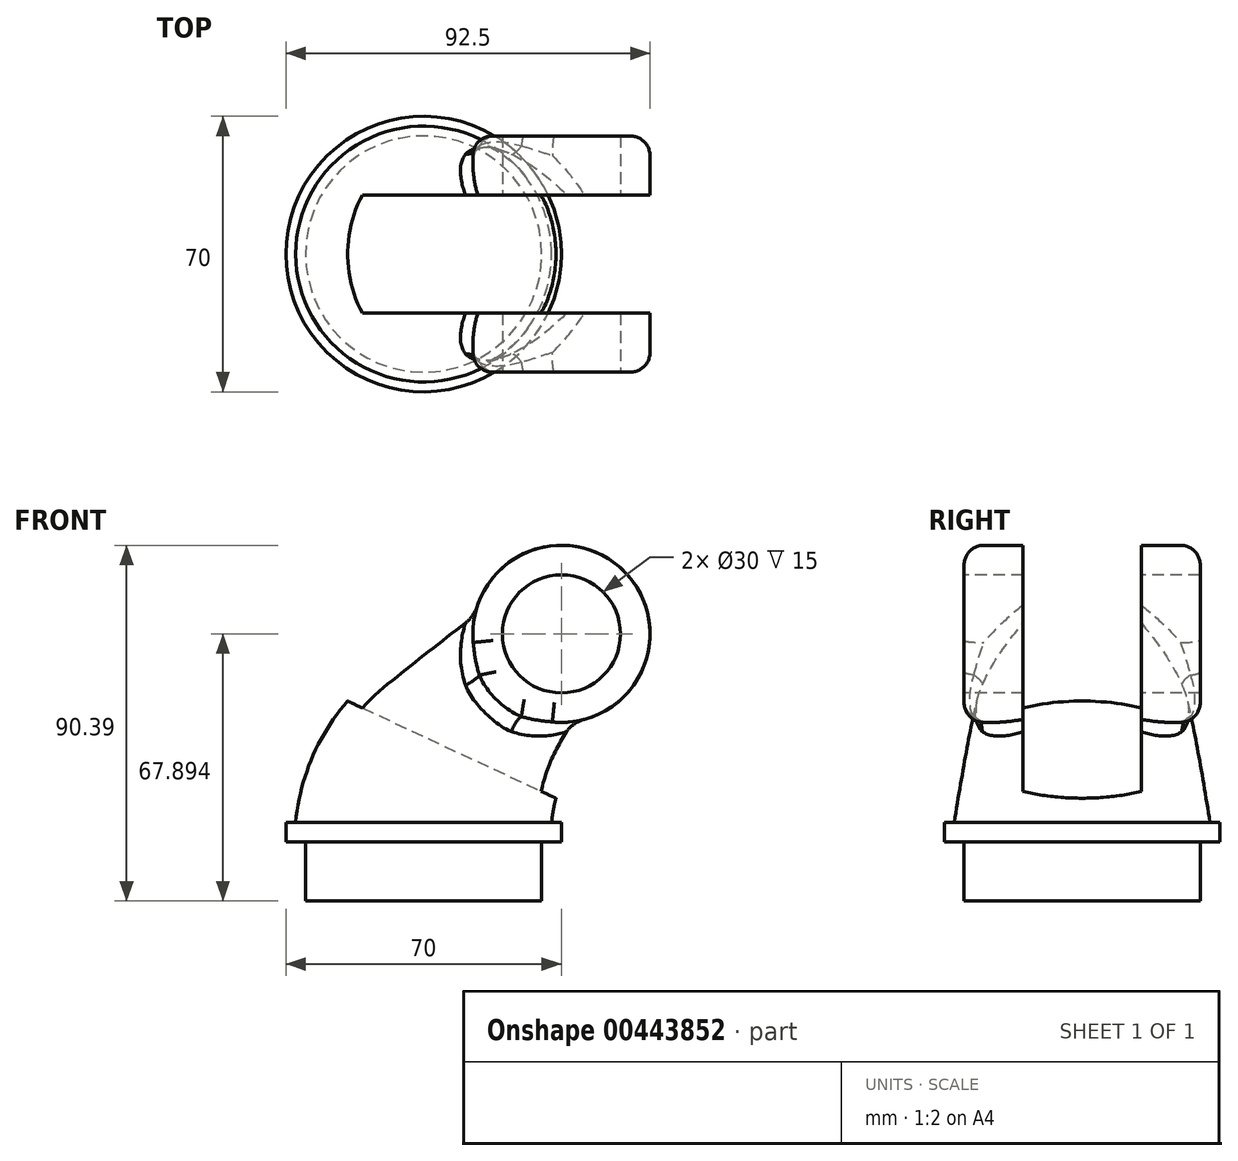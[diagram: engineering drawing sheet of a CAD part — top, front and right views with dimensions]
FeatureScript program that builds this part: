
annotation { "Feature Type Name" : "Feature", "Feature Type Description" : "" }
export const myFeature = defineFeature(function(context is Context, id is Id, definition is map)
    precondition{}
    {
        {
            var Q0;
            Q0=qCreatedBy(makeId("Top.planeOp"),FACE);
            var sketch = newSketch(context, id + "F0", { "sketchPlane" : qUnion([Q0])});
            skCircle(sketch, "E0", {"center": v(0, 0) * mm, "radius": 35 * mm});
            skSolve(sketch);
        }
        {
            var Q0;
            Q0 = qSketchRegion(id + "F0", true);
            extrude(context, id + "F1", {"entities" : qUnion([Q0]), "depth" : 5 * mm});
        }
        {
            var Q0;
            Q0=qCreatedBy(makeId("Front.planeOp"),FACE);
            var sketch = newSketch(context, id + "F2", { "sketchPlane" : qUnion([Q0])});
            skArc(sketch, "E1", {"start": v(17.6, 38.3) * mm, "mid": v(5.55, 23.37) * mm, "end": v(0, 5) * mm});
            skLineSegment(sketch, "E2", {"start": v(17.6, 38.3) * mm, "end": v(35, 52.9) * mm});
            skSolve(sketch);
        }
        {
            var Q0;
            Q0=sQuery(id+"F2.wireOp",VERTEX,"E2.end");
            var Q1;
            Q1=sQuery(id+"F2.wireOp",EDGE,"E2");
            cPlane(context, id + "F3", {"entities" : qUnion([Q0, Q1]), "cplaneType" : CPlaneType.LINE_POINT, "offset" : 25 * mm, "width" : 150 * mm, "height" : 150 * mm});
        }
        {
            var Q0;
            Q0=qCreatedBy(id+"F3.planeOp",FACE);
            var sketch = newSketch(context, id + "F4", { "sketchPlane" : qUnion([Q0])});
            skCircle(sketch, "E3", {"center": v(0, 18.02) * mm, "radius": 22.5 * mm});
            skSolve(sketch);
        }
        {
            var Q0;
            Q0=makeQuery(id+"F1.opExtrude","CAP_FACE",FACE,{"disambiguationData":[OSD([sQuery(id+"F0.wireOp",EDGE,"E0")])],"isStart":false});
            var sketch = newSketch(context, id + "F5", { "sketchPlane" : qUnion([Q0])});
            skCircle(sketch, "E4", {"center": v(0, 0) * mm, "radius": 32.5 * mm});
            skSolve(sketch);
        }
        {
            var Q0;
            Q0=qCreatedBy(makeId("Front.planeOp"),FACE);
            var sketch = newSketch(context, id + "F6", { "sketchPlane" : qUnion([Q0])});
            skArc(sketch, "E5", {"start": v(-13.25, 41.78) * mm, "mid": v(-26.5, 25.3) * mm, "end": v(-32.5, 5) * mm});
            skLineSegment(sketch, "E6", {"start": v(-13.25, 41.78) * mm, "end": v(20.54, 70.13) * mm});
            skSolve(sketch);
        }
        {
            var Q0;
            Q0=qCreatedBy(makeId("Front.planeOp"),FACE);
            var sketch = newSketch(context, id + "F7", { "sketchPlane" : qUnion([Q0])});
            skArc(sketch, "E7", {"start": v(48.46, 34.82) * mm, "mid": v(37.6, 21.45) * mm, "end": v(32.5, 5) * mm});
            skLineSegment(sketch, "E8", {"start": v(48.46, 34.82) * mm, "end": v(49.46, 35.66) * mm});
            skSolve(sketch);
        }
        {
            var Q1;
            Q1=makeQuery(id+"F4.imprint","IMPRINT",FACE,{"disambiguationData":[TD([[makeQuery(id+"F4.imprint","IMPRINT",EDGE,{"derivedFrom":sQuery(id+"F4.wireOp",EDGE,"E3")}),1.0]])]});
            var Q2;
            Q2=makeQuery(id+"F5.imprint","IMPRINT",FACE,{"disambiguationData":[TD([[makeQuery(id+"F5.imprint","IMPRINT",EDGE,{"derivedFrom":sQuery(id+"F5.wireOp",EDGE,"E4")}),1.0]])]});
            var Q3;
            Q3 = qConstructionFilter(qBodyType(qCreatedBy(id + "F7" ,EDGE), BodyType.WIRE), ConstructionObject.NO);
            var Q4;
            Q4 = qConstructionFilter(qBodyType(qCreatedBy(id + "F6" ,EDGE), BodyType.WIRE), ConstructionObject.NO);
            loft(context, id + "F8", {"operationType" : NewBodyOperationType.ADD, "addGuides" : true, "sheetProfilesArray" : [{ "sheetProfileEntities" : qUnion([Q1]) }, { "sheetProfileEntities" : qUnion([Q2]) }], "guidesArray" : [{ "guideEntities" : qUnion([Q3]), "guideDerivativeType" : LoftGuideDerivativeType.DEFAULT, "guideDerivativeMagnitude" : 1 }, { "guideEntities" : qUnion([Q4]), "guideDerivativeType" : LoftGuideDerivativeType.DEFAULT, "guideDerivativeMagnitude" : 1 }]});
        }
        {
            var Q0;
            Q0=qCreatedBy(makeId("Front.planeOp"),FACE);
            var sketch = newSketch(context, id + "F9", { "sketchPlane" : qUnion([Q0])});
            skCircle(sketch, "E9", {"center": v(35, 52.9) * mm, "radius": 22.5 * mm});
            skSolve(sketch);
        }
        {
            var Q0;
            Q0 = qSketchRegion(id + "F9", true);
            extrude(context, id + "F10", {"entities" : qUnion([Q0]), "operationType" : NewBodyOperationType.ADD, "endBound" : BoundingType.SYMMETRIC, "depth" : 60 * mm});
        }
        {
            var Q0;
            Q0=makeQuery(id+"F10.boolean.opBoolean","INTERSECT",EDGE,{"disambiguationData":[OD(0.0)],"derivedFrom":[makeQuery(id+"F8.opLoft","SWEPT_FACE",FACE,{"disambiguationData":[OSD([sQuery(id+"F4.wireOp",EDGE,"E3"),sQuery(id+"F5.wireOp",EDGE,"E4"),sQuery(id+"F6.wireOp",VERTEX,"E6.start"),sQuery(id+"F6.wireOp",EDGE,"E5"),sQuery(id+"F6.wireOp",EDGE,"E6"),sQuery(id+"F7.wireOp",VERTEX,"E8.start"),sQuery(id+"F7.wireOp",EDGE,"E7"),sQuery(id+"F7.wireOp",EDGE,"E8")])]}),makeQuery(id+"F10.opExtrude","SWEPT_FACE",FACE,{"disambiguationData":[OSD([sQuery(id+"F9.wireOp",EDGE,"E9")])]})]});
            var Q1;
            Q1=makeQuery(id+"F10.boolean.opBoolean","INTERSECT",EDGE,{"disambiguationData":[OD(1.0)],"derivedFrom":[makeQuery(id+"F8.opLoft","SWEPT_FACE",FACE,{"disambiguationData":[OSD([sQuery(id+"F4.wireOp",EDGE,"E3"),sQuery(id+"F5.wireOp",EDGE,"E4"),sQuery(id+"F6.wireOp",VERTEX,"E6.start"),sQuery(id+"F6.wireOp",EDGE,"E5"),sQuery(id+"F6.wireOp",EDGE,"E6"),sQuery(id+"F7.wireOp",VERTEX,"E8.start"),sQuery(id+"F7.wireOp",EDGE,"E7"),sQuery(id+"F7.wireOp",EDGE,"E8")])]}),makeQuery(id+"F10.opExtrude","SWEPT_FACE",FACE,{"disambiguationData":[OSD([sQuery(id+"F9.wireOp",EDGE,"E9")])]})]});
            fillet(context, id + "F11", {"entities" : qUnion([Q0, Q1]), "radius" : 5 * mm, "tangentPropagation" : true, "allowEdgeOverflow" : false});
        }
        {
            var Q0;
            Q0=makeQuery(id+"F10.opExtrude","CAP_EDGE",EDGE,{"disambiguationData":[OSD([sQuery(id+"F9.wireOp",EDGE,"E9")])],"isStart":false});
            var Q1;
            Q1=makeQuery(id+"F10.opExtrude","CAP_EDGE",EDGE,{"disambiguationData":[OSD([sQuery(id+"F9.wireOp",EDGE,"E9")])],"isStart":true});
            var Q2;
            Q2=makeQuery(id+"F10.opExtrude","CAP_FACE",FACE,{"disambiguationData":[OSD([sQuery(id+"F9.wireOp",EDGE,"E9")])],"isStart":false});
            fillet(context, id + "F12", {"entities" : qUnion([Q0, Q1, Q2]), "radius" : 5 * mm, "tangentPropagation" : true, "allowEdgeOverflow" : false});
        }
        {
            var Q0;
            Q0=makeQuery(id+"F10.opExtrude","CAP_FACE",FACE,{"disambiguationData":[OSD([sQuery(id+"F9.wireOp",EDGE,"E9")])],"isStart":false});
            var sketch = newSketch(context, id + "F13", { "sketchPlane" : qUnion([Q0])});
            skCircle(sketch, "E10", {"center": v(35, 52.9) * mm, "radius": 15 * mm});
            skSolve(sketch);
        }
        {
            var Q0;
            Q0 = qSketchRegion(id + "F13", true);
            extrude(context, id + "F14", {"entities" : qUnion([Q0]), "operationType" : NewBodyOperationType.REMOVE, "endBound" : BoundingType.THROUGH_ALL, "oppositeDirection" : true, "depth" : 25 * mm});
        }
        {
            var Q0;
            Q0=qCreatedBy(makeId("Front.planeOp"),FACE);
            var sketch = newSketch(context, id + "F15", { "sketchPlane" : qUnion([Q0])});
            skLineSegment(sketch, "E11", {"start": v(-104.18, 75.4) * mm, "end": v(57.5, 0) * mm});
            skLineSegment(sketch, "E12", {"start": v(57.5, 75.4) * mm, "end": v(57.5, 0) * mm});
            skLineSegment(sketch, "E13", {"start": v(-104.18, 75.4) * mm, "end": v(57.5, 75.4) * mm});
            skSolve(sketch);
        }
        {
            var Q0;
            Q0=makeQuery(id+"F15.imprint","IMPRINT",FACE,{"disambiguationData":[TD([[makeQuery(id+"F15.imprint","IMPRINT",EDGE,{"derivedFrom":sQuery(id+"F15.wireOp",EDGE,"E11")}),1.0]])]});
            extrude(context, id + "F16", {"entities" : qUnion([Q0]), "operationType" : NewBodyOperationType.REMOVE, "endBound" : BoundingType.SYMMETRIC, "oppositeDirection" : true, "depth" : 30 * mm});
        }
        {
            var Q0;
            Q0=qCreatedBy(makeId("Front.planeOp"),FACE);
            var sketch = newSketch(context, id + "F17", { "sketchPlane" : qUnion([Q0])});
            skPoint(sketch, "E14.middle", {"position": v(0, 0) * mm});
            skLineSegment(sketch, "E15.bottom", {"start": v(0, 0) * mm, "end": v(-30, 0) * mm});
            skLineSegment(sketch, "E15.top", {"start": v(0, -15) * mm, "end": v(-30, -15) * mm});
            skLineSegment(sketch, "E15.left", {"start": v(0, 0) * mm, "end": v(0, -15) * mm});
            skLineSegment(sketch, "E15.right", {"start": v(-30, 0) * mm, "end": v(-30, -15) * mm});
            skSolve(sketch);
        }
        {
            var Q0;
            Q0=makeQuery(id+"F17.imprint","IMPRINT",FACE,{"disambiguationData":[TD([[makeQuery(id+"F17.imprint","IMPRINT",EDGE,{"derivedFrom":sQuery(id+"F17.wireOp",EDGE,"E15.bottom")}),1.0]])]});
            var Q1;
            Q1=sQuery(id+"F17.wireOp",EDGE,"E15.left");
            revolve(context, id + "F18", {"operationType" : NewBodyOperationType.ADD, "entities" : qUnion([Q0]), "axis" : qUnion([Q1]), "revolveType" : RevolveType.FULL});
        }
    });
